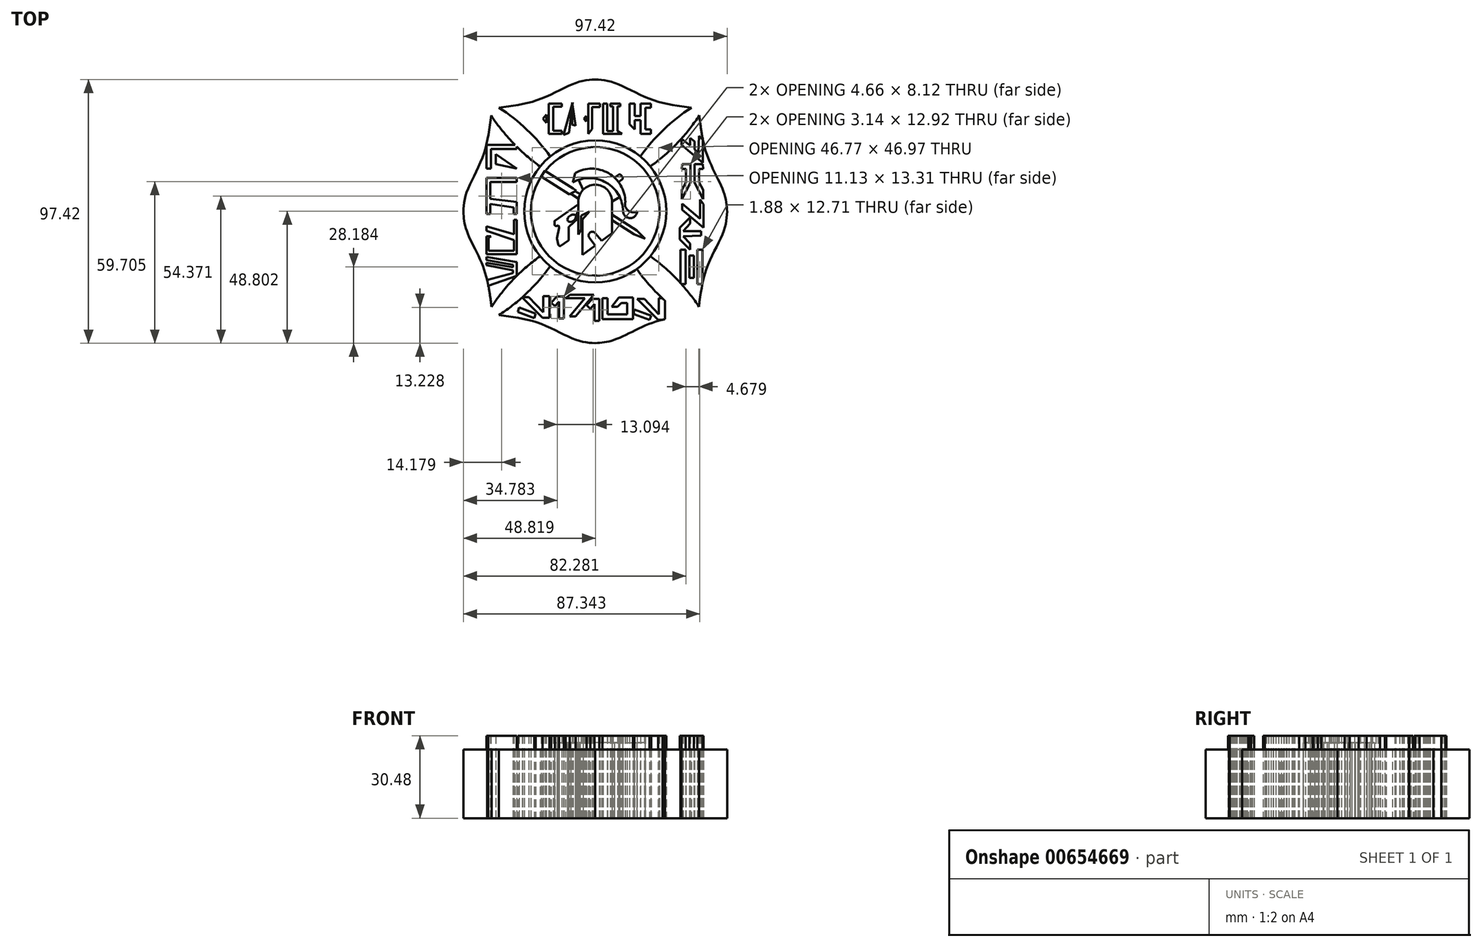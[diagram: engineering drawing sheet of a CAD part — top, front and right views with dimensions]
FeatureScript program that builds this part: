
annotation { "Feature Type Name" : "Feature", "Feature Type Description" : "" }
export const myFeature = defineFeature(function(context is Context, id is Id, definition is map)
    precondition{}
    {
        {
            var Q0;
            Q0=qCreatedBy(makeId("Top.planeOp"),FACE);
            var sketch = newSketch(context, id + "F0", { "sketchPlane" : qUnion([Q0])});
            skCircle(sketch, "E0", {"center": v(0, 0) * mm, "radius": 26.23 * mm});
            skCircle(sketch, "E1", {"center": v(0, 0) * mm, "radius": 23.74 * mm});
            skArc(sketch, "E2", {"start": v(35.51, 38.32) * mm, "mid": v(25.23, 30.18) * mm, "end": v(16.63, 20.3) * mm});
            skArc(sketch, "E3.MirrorCS", {"start": v(38.41, 35.41) * mm, "mid": v(30.25, 25.15) * mm, "end": v(20.34, 16.57) * mm});
            skArc(sketch, "E4.MirrorCS", {"start": v(-35.51, 38.32) * mm, "mid": v(-25.23, 30.18) * mm, "end": v(-16.63, 20.3) * mm});
            skArc(sketch, "E5.MirrorCS", {"start": v(-38.41, 35.41) * mm, "mid": v(-30.25, 25.15) * mm, "end": v(-20.34, 16.57) * mm});
            skArc(sketch, "E6.MirrorCS", {"start": v(-35.51, -38.32) * mm, "mid": v(-25.23, -30.18) * mm, "end": v(-16.63, -20.3) * mm});
            skArc(sketch, "E7.MirrorCS", {"start": v(-38.41, -35.41) * mm, "mid": v(-30.25, -25.15) * mm, "end": v(-20.34, -16.57) * mm});
            skArc(sketch, "E8.MirrorCS", {"start": v(38.41, -35.41) * mm, "mid": v(30.25, -25.15) * mm, "end": v(20.34, -16.57) * mm});
            skFitSpline(sketch, "E9", {"points": [v(-35.51, 38.32) * mm, v(-20.45, 41.42) * mm, v(-6.98, 47.51) * mm, v(0, 48.72) * mm], "startDerivative": vector(40.3, 5.04) * mm, "endDerivative": vector(25.56, 1.65) * mm});
            skFitSpline(sketch, "E10.MirrorCS", {"points": [v(35.51, 38.32) * mm, v(20.45, 41.42) * mm, v(6.98, 47.51) * mm, v(0, 48.72) * mm], "startDerivative": vector(-40.3, 5.04) * mm, "endDerivative": vector(-25.56, 1.65) * mm});
            skFitSpline(sketch, "E11.MirrorCS", {"points": [v(38.41, 35.41) * mm, v(41.47, 20.34) * mm, v(47.53, 6.86) * mm, v(48.72, -0.14) * mm], "startDerivative": vector(4.94, -40.31) * mm, "endDerivative": vector(1.58, -25.56) * mm});
            skFitSpline(sketch, "E12.MirrorCS", {"points": [v(38.23, -35.61) * mm, v(41.37, -20.55) * mm, v(47.5, -7.1) * mm, v(48.72, -0.12) * mm], "startDerivative": vector(5.15, 40.29) * mm, "endDerivative": vector(1.72, 25.55) * mm});
            skArc(sketch, "E13.MirrorCS", {"start": v(34.27, -39.56) * mm, "mid": v(24, -31.4) * mm, "end": v(15.43, -21.48) * mm});
            skFitSpline(sketch, "E14.MirrorCS", {"points": [v(35.51, -38.32) * mm, v(20.45, -41.42) * mm, v(6.98, -47.51) * mm, v(0, -48.72) * mm], "startDerivative": vector(-40.3, -5.04) * mm, "endDerivative": vector(-25.56, -1.65) * mm});
            skFitSpline(sketch, "E15.MirrorCS", {"points": [v(-35.51, -38.32) * mm, v(-20.45, -41.42) * mm, v(-6.98, -47.51) * mm, v(0, -48.72) * mm], "startDerivative": vector(40.3, -5.04) * mm, "endDerivative": vector(25.56, -1.65) * mm});
            skFitSpline(sketch, "E16.MirrorCS", {"points": [v(-38.23, -35.61) * mm, v(-41.37, -20.55) * mm, v(-47.5, -7.1) * mm, v(-48.72, -0.12) * mm], "startDerivative": vector(-5.15, 40.29) * mm, "endDerivative": vector(-1.72, 25.55) * mm});
            skFitSpline(sketch, "E17.MirrorCS", {"points": [v(-38.41, 35.41) * mm, v(-41.47, 20.34) * mm, v(-47.53, 6.86) * mm, v(-48.72, -0.14) * mm], "startDerivative": vector(-4.94, -40.31) * mm, "endDerivative": vector(-1.58, -25.56) * mm});
            skLineSegment(sketch, "E18.left", {"start": v(-6.25, 3.57) * mm, "end": v(-6.25, -8.57) * mm});
            skLineSegment(sketch, "E18.right", {"start": v(6.25, 3.57) * mm, "end": v(6.25, -8.06) * mm});
            skPoint(sketch, "E18.middle", {"position": v(0, -8.06) * mm});
            skArc(sketch, "E19", {"start": v(6.25, 3.57) * mm, "mid": v(0, 9.82) * mm, "end": v(-6.25, 3.57) * mm});
            skLineSegment(sketch, "E20", {"start": v(-4.67, -16.13) * mm, "end": v(0, -12.68) * mm});
            skLineSegment(sketch, "E21", {"start": v(2.37, -10.93) * mm, "end": v(0, -8.06) * mm});
            skLineSegment(sketch, "E22", {"start": v(0, -12.68) * mm, "end": v(-2.14, -9.78) * mm});
            skArc(sketch, "E23", {"start": v(0, -8.06) * mm, "mid": v(-1.93, -7.85) * mm, "end": v(-2.14, -9.78) * mm});
            skPoint(sketch, "E23.third.point", {"position": v(0, -9.78) * mm});
            skLineSegment(sketch, "E24.trimOffspring", {"start": v(2.37, -10.93) * mm, "end": v(6.25, -8.06) * mm});
            skPoint(sketch, "E18.top.end.orphan", {"position": v(6.25, -19.7) * mm});
            skPoint(sketch, "E25.orphan", {"position": v(-6.25, -19.7) * mm});
            skArc(sketch, "E26", {"start": v(11.12, 3.49) * mm, "mid": v(4.91, 14.1) * mm, "end": v(-7.38, 14.17) * mm});
            skArc(sketch, "E27", {"start": v(10.28, 0.03) * mm, "mid": v(4.07, 10.64) * mm, "end": v(-8.22, 10.7) * mm});
            skLineSegment(sketch, "E28", {"start": v(-8.22, 10.7) * mm, "end": v(-7.38, 14.17) * mm});
            skArc(sketch, "E29", {"start": v(11.12, 3.49) * mm, "mid": v(12.15, 0.3) * mm, "end": v(15.48, 0.03) * mm});
            skArc(sketch, "E30", {"start": v(10.28, 0.03) * mm, "mid": v(12.88, -2.5) * mm, "end": v(15.48, 0.03) * mm});
            skLineSegment(sketch, "E31", {"start": v(15.43, -21.48) * mm, "end": v(15.3, -21.3) * mm});
            skLineSegment(sketch, "E32", {"start": v(-4.67, -16.13) * mm, "end": v(-4.67, -2.97) * mm});
            skLineSegment(sketch, "E33", {"start": v(-4.67, -2.97) * mm, "end": v(-2.14, -0.12) * mm});
            skLineSegment(sketch, "E34", {"start": v(-2.14, -0.12) * mm, "end": v(-5.26, -1.55) * mm});
            skPoint(sketch, "E34.endSnap0", {"position": v(-3.4, -1.55) * mm});
            skLineSegment(sketch, "E35", {"start": v(-5.26, -1.55) * mm, "end": v(-5.26, -6.86) * mm});
            skPoint(sketch, "E35.endSnap0", {"position": v(-6.25, -6.86) * mm});
            skLineSegment(sketch, "E36", {"start": v(-5.26, -6.86) * mm, "end": v(-6.25, -8.57) * mm});
            skPoint(sketch, "E37.orphan", {"position": v(-6.25, -17.3) * mm});
            skLineSegment(sketch, "E38", {"start": v(-4.46, 7.95) * mm, "end": v(-6.14, 11.64) * mm});
            skLineSegment(sketch, "E39", {"start": v(6.25, 3.57) * mm, "end": v(9.04, 5.3) * mm});
            skLineSegment(sketch, "E40.bottom", {"start": v(-12.4, 39.78) * mm, "end": v(-17.13, 39.78) * mm});
            skLineSegment(sketch, "E40.top", {"start": v(-12.4, 38.6) * mm, "end": v(-15.49, 38.6) * mm});
            skLineSegment(sketch, "E40.left", {"start": v(-12.4, 39.78) * mm, "end": v(-12.4, 38.6) * mm});
            skLineSegment(sketch, "E40.right", {"start": v(-17.13, 39.78) * mm, "end": v(-17.13, 38.6) * mm});
            skLineSegment(sketch, "E41.bottom", {"start": v(-17.13, 39.78) * mm, "end": v(-15.49, 39.78) * mm});
            skLineSegment(sketch, "E41.left", {"start": v(-17.13, 39.78) * mm, "end": v(-17.13, 34.21) * mm});
            skLineSegment(sketch, "E41.right", {"start": v(-15.49, 38.6) * mm, "end": v(-15.49, 34.21) * mm});
            skLineSegment(sketch, "E42.bottom", {"start": v(-2.52, 39.78) * mm, "end": v(-1.13, 39.78) * mm});
            skLineSegment(sketch, "E42.left", {"start": v(-2.52, 39.78) * mm, "end": v(-2.52, 34.21) * mm});
            skLineSegment(sketch, "E42.right", {"start": v(-1.13, 38.54) * mm, "end": v(-1.13, 34.21) * mm});
            skLineSegment(sketch, "E43.bottom", {"start": v(-2.52, 39.78) * mm, "end": v(1.82, 39.78) * mm});
            skLineSegment(sketch, "E43.top", {"start": v(-1.13, 38.54) * mm, "end": v(1.82, 38.54) * mm});
            skLineSegment(sketch, "E43.left", {"start": v(-2.52, 39.78) * mm, "end": v(-2.52, 38.54) * mm});
            skLineSegment(sketch, "E43.right", {"start": v(1.82, 39.78) * mm, "end": v(1.82, 38.54) * mm});
            skLineSegment(sketch, "E44", {"start": v(-8.28, 40.2) * mm, "end": v(-8.4, 39.75) * mm});
            skLineSegment(sketch, "E45", {"start": v(-11.7, 28.2) * mm, "end": v(-9.65, 28.98) * mm});
            skLineSegment(sketch, "E46", {"start": v(-9.65, 28.98) * mm, "end": v(-8.48, 38.58) * mm});
            skLineSegment(sketch, "E47", {"start": v(-8.48, 40.2) * mm, "end": v(-8.48, 39.51) * mm});
            skLineSegment(sketch, "E48", {"start": v(-8.48, 32.05) * mm, "end": v(-7.25, 31.7) * mm});
            skLineSegment(sketch, "E49", {"start": v(-7.25, 31.7) * mm, "end": v(-8.37, 39.46) * mm});
            skLineSegment(sketch, "E50.MirrorCS", {"start": v(-12.4, 28.65) * mm, "end": v(-17.13, 28.65) * mm});
            skLineSegment(sketch, "E51.MirrorCS", {"start": v(-12.4, 29.82) * mm, "end": v(-15.49, 29.82) * mm});
            skLineSegment(sketch, "E52.MirrorCS", {"start": v(-12.4, 28.65) * mm, "end": v(-12.4, 29.82) * mm});
            skLineSegment(sketch, "E53.MirrorCS", {"start": v(-17.13, 28.65) * mm, "end": v(-17.13, 34.21) * mm});
            skLineSegment(sketch, "E54.MirrorCS", {"start": v(-15.49, 29.82) * mm, "end": v(-15.49, 34.21) * mm});
            skLineSegment(sketch, "E55.MirrorCS", {"start": v(-2.52, 28.65) * mm, "end": v(-2.52, 34.21) * mm});
            skLineSegment(sketch, "E56.MirrorCS", {"start": v(-1.13, 30.44) * mm, "end": v(-1.13, 34.21) * mm});
            skLineSegment(sketch, "E57", {"start": v(-2.52, 28.65) * mm, "end": v(-1.13, 30.44) * mm});
            skPoint(sketch, "E58.orphan", {"position": v(-1.13, 28.65) * mm});
            skPoint(sketch, "E59.orphan", {"position": v(10.7, 28.65) * mm});
            skPoint(sketch, "E60.orphan", {"position": v(10.28, 29.44) * mm});
            skLineSegment(sketch, "E61", {"start": v(-3.29, 35.2) * mm, "end": v(-3.29, 34.21) * mm});
            skPoint(sketch, "E61.endSnap0", {"position": v(-18.03, 34.21) * mm});
            skLineSegment(sketch, "E62", {"start": v(-4.27, 34.21) * mm, "end": v(-3.29, 35.2) * mm});
            skLineSegment(sketch, "E63.MirrorCS", {"start": v(-3.29, 33.23) * mm, "end": v(-3.29, 34.21) * mm});
            skLineSegment(sketch, "E64.MirrorCS", {"start": v(-4.27, 34.21) * mm, "end": v(-3.29, 33.23) * mm});
            skLineSegment(sketch, "E65", {"start": v(-18.03, 35.71) * mm, "end": v(-19.33, 34.21) * mm});
            skLineSegment(sketch, "E66", {"start": v(-18.03, 34.21) * mm, "end": v(-18.03, 35.71) * mm});
            skLineSegment(sketch, "E67", {"start": v(-18.03, 34.21) * mm, "end": v(-18.03, 32.71) * mm});
            skLineSegment(sketch, "E68", {"start": v(-18.03, 32.71) * mm, "end": v(-19.33, 34.21) * mm});
            skLineSegment(sketch, "E69.bottom", {"start": v(2.96, 39.78) * mm, "end": v(4.44, 39.78) * mm});
            skLineSegment(sketch, "E69.top", {"start": v(2.96, 28.65) * mm, "end": v(4.44, 28.65) * mm});
            skLineSegment(sketch, "E69.left", {"start": v(2.96, 39.78) * mm, "end": v(2.96, 28.65) * mm});
            skLineSegment(sketch, "E69.right", {"start": v(4.44, 39.78) * mm, "end": v(4.44, 29.7) * mm});
            skLineSegment(sketch, "E70.bottom", {"start": v(2.96, 28.65) * mm, "end": v(8.18, 28.65) * mm});
            skLineSegment(sketch, "E70.top", {"start": v(4.44, 29.7) * mm, "end": v(6.61, 29.7) * mm});
            skLineSegment(sketch, "E70.left", {"start": v(2.96, 28.65) * mm, "end": v(2.96, 29.7) * mm});
            skLineSegment(sketch, "E71.bottom", {"start": v(8.18, 28.65) * mm, "end": v(6.61, 28.65) * mm});
            skLineSegment(sketch, "E71.top", {"start": v(8.18, 39.78) * mm, "end": v(6.61, 39.78) * mm});
            skLineSegment(sketch, "E71.left", {"start": v(8.18, 29.7) * mm, "end": v(8.18, 38.83) * mm});
            skLineSegment(sketch, "E71.right", {"start": v(6.61, 29.7) * mm, "end": v(6.61, 38.83) * mm});
            skLineSegment(sketch, "E72.bottom", {"start": v(5.53, 39.78) * mm, "end": v(9.3, 39.78) * mm});
            skLineSegment(sketch, "E72.top", {"start": v(5.53, 38.83) * mm, "end": v(6.61, 38.83) * mm});
            skLineSegment(sketch, "E72.left", {"start": v(5.53, 39.78) * mm, "end": v(5.53, 38.83) * mm});
            skLineSegment(sketch, "E72.right", {"start": v(9.3, 39.78) * mm, "end": v(9.3, 38.83) * mm});
            skLineSegment(sketch, "E73", {"start": v(8.18, 29.7) * mm, "end": v(9.87, 28.65) * mm});
            skLineSegment(sketch, "E74", {"start": v(9.87, 28.65) * mm, "end": v(8.18, 28.65) * mm});
            skLineSegment(sketch, "E75.trimOffspring", {"start": v(8.18, 38.83) * mm, "end": v(9.3, 38.83) * mm});
            skLineSegment(sketch, "E76", {"start": v(12.66, 39.78) * mm, "end": v(14.62, 39.78) * mm});
            skLineSegment(sketch, "E77.left", {"start": v(12.66, 39.78) * mm, "end": v(12.66, 32.13) * mm});
            skLineSegment(sketch, "E77.right", {"start": v(14.62, 39.78) * mm, "end": v(14.62, 35.22) * mm});
            skLineSegment(sketch, "E78.bottom", {"start": v(14.62, 35.22) * mm, "end": v(16.76, 35.22) * mm});
            skLineSegment(sketch, "E78.top", {"start": v(14.62, 33.67) * mm, "end": v(16.76, 33.67) * mm});
            skLineSegment(sketch, "E78.left", {"start": v(12.66, 35.22) * mm, "end": v(12.66, 33.67) * mm});
            skLineSegment(sketch, "E79.bottom", {"start": v(16.76, 39.78) * mm, "end": v(18.48, 39.78) * mm});
            skLineSegment(sketch, "E79.top", {"start": v(16.76, 28.65) * mm, "end": v(18.48, 28.65) * mm});
            skLineSegment(sketch, "E79.left", {"start": v(16.76, 39.78) * mm, "end": v(16.76, 35.22) * mm});
            skLineSegment(sketch, "E79.right", {"start": v(18.48, 38.24) * mm, "end": v(18.48, 30.3) * mm});
            skLineSegment(sketch, "E80.bottom", {"start": v(16.76, 39.78) * mm, "end": v(20.61, 39.78) * mm});
            skLineSegment(sketch, "E80.top", {"start": v(18.48, 38.24) * mm, "end": v(20.61, 38.24) * mm});
            skLineSegment(sketch, "E80.left", {"start": v(16.76, 39.78) * mm, "end": v(16.76, 38.24) * mm});
            skLineSegment(sketch, "E80.right", {"start": v(20.61, 39.78) * mm, "end": v(20.61, 38.24) * mm});
            skLineSegment(sketch, "E81.bottom", {"start": v(16.76, 28.65) * mm, "end": v(20.61, 28.65) * mm});
            skLineSegment(sketch, "E81.top", {"start": v(18.48, 30.3) * mm, "end": v(20.61, 30.3) * mm});
            skLineSegment(sketch, "E81.left", {"start": v(16.76, 28.65) * mm, "end": v(16.76, 30.3) * mm});
            skLineSegment(sketch, "E81.right", {"start": v(20.61, 28.65) * mm, "end": v(20.61, 30.3) * mm});
            skLineSegment(sketch, "E82.trimOffspring", {"start": v(18.48, 28.65) * mm, "end": v(20.61, 28.65) * mm});
            skLineSegment(sketch, "E83", {"start": v(12.66, 32.13) * mm, "end": v(14.62, 30.23) * mm});
            skLineSegment(sketch, "E84.trimOffspring", {"start": v(16.76, 33.67) * mm, "end": v(16.76, 28.65) * mm});
            skLineSegment(sketch, "E85.trimOffspring", {"start": v(14.62, 33.67) * mm, "end": v(14.62, 30.23) * mm});
            skLineSegment(sketch, "E86.trimOffspring", {"start": v(-8.4, 39.75) * mm, "end": v(-8.48, 40.2) * mm});
            skLineSegment(sketch, "E87.trimOffspring", {"start": v(-8.48, 39.51) * mm, "end": v(-11.7, 28.2) * mm});
            skLineSegment(sketch, "E88.trimOffspring", {"start": v(-8.37, 39.46) * mm, "end": v(-8.28, 40.2) * mm});
            skLineSegment(sketch, "E89.trimOffspring", {"start": v(-8.48, 38.58) * mm, "end": v(-8.48, 32.05) * mm});
            skLineSegment(sketch, "E90", {"start": v(-28.97, -18.8) * mm, "end": v(-40.1, -16.82) * mm});
            skLineSegment(sketch, "E91", {"start": v(-40.1, -16.82) * mm, "end": v(-40.1, -18.04) * mm});
            skLineSegment(sketch, "E92", {"start": v(-40.1, -18.04) * mm, "end": v(-30.4, -19.76) * mm});
            skLineSegment(sketch, "E93", {"start": v(-30.4, -19.76) * mm, "end": v(-30.4, -20.72) * mm});
            skLineSegment(sketch, "E94", {"start": v(-30.4, -20.72) * mm, "end": v(-40.1, -19) * mm});
            skLineSegment(sketch, "E95", {"start": v(-40.1, -19) * mm, "end": v(-40.1, -19.9) * mm});
            skLineSegment(sketch, "E96", {"start": v(-40.1, -19.9) * mm, "end": v(-30.32, -21.8) * mm});
            skLineSegment(sketch, "E97", {"start": v(-30.32, -21.8) * mm, "end": v(-30.32, -22.87) * mm});
            skLineSegment(sketch, "E98", {"start": v(-30.32, -22.87) * mm, "end": v(-40.1, -25.47) * mm});
            skLineSegment(sketch, "E99", {"start": v(-40.1, -25.47) * mm, "end": v(-40.1, -27.73) * mm});
            skLineSegment(sketch, "E100", {"start": v(-40.1, -27.73) * mm, "end": v(-28.97, -23.85) * mm});
            skLineSegment(sketch, "E101", {"start": v(-28.97, -23.85) * mm, "end": v(-28.97, -18.8) * mm});
            skLineSegment(sketch, "E102.bottom", {"start": v(-40.1, -15.83) * mm, "end": v(-40.1, -14.56) * mm});
            skLineSegment(sketch, "E102.left", {"start": v(-40.1, -15.83) * mm, "end": v(-28.97, -15.83) * mm});
            skLineSegment(sketch, "E102.right", {"start": v(-39.41, -14.56) * mm, "end": v(-30.02, -14.56) * mm});
            skLineSegment(sketch, "E103.bottom", {"start": v(-28.97, -15.83) * mm, "end": v(-28.97, -3.12) * mm});
            skLineSegment(sketch, "E103.top", {"start": v(-30.02, -14.56) * mm, "end": v(-30.02, -10.64) * mm});
            skLineSegment(sketch, "E103.left", {"start": v(-28.97, -15.83) * mm, "end": v(-30.02, -15.83) * mm});
            skLineSegment(sketch, "E103.right", {"start": v(-28.97, -3.12) * mm, "end": v(-30.02, -3.12) * mm});
            skLineSegment(sketch, "E104.left", {"start": v(-38.1, -6.34) * mm, "end": v(-38.11, -6.34) * mm});
            skLineSegment(sketch, "E104.right", {"start": v(-38.1, -5.52) * mm, "end": v(-38.11, -5.52) * mm});
            skLineSegment(sketch, "E105.bottom", {"start": v(-40.1, -15.83) * mm, "end": v(-40.1, -9.27) * mm});
            skLineSegment(sketch, "E105.top", {"start": v(-39.41, -14.56) * mm, "end": v(-39.41, -9.91) * mm});
            skLineSegment(sketch, "E105.left", {"start": v(-40.1, -15.83) * mm, "end": v(-39.41, -15.83) * mm});
            skLineSegment(sketch, "E105.right", {"start": v(-40.1, -9.27) * mm, "end": v(-39.41, -9.27) * mm});
            skLineSegment(sketch, "E106", {"start": v(-40.1, -9.27) * mm, "end": v(-38.43, -9.27) * mm});
            skPoint(sketch, "E106.endSnap0", {"position": v(-39.75, -9.27) * mm});
            skLineSegment(sketch, "E107", {"start": v(-38.43, -9.27) * mm, "end": v(-39.41, -9.91) * mm});
            skLineSegment(sketch, "E108", {"start": v(-30.02, -10.64) * mm, "end": v(-40.1, -7.24) * mm});
            skLineSegment(sketch, "E109", {"start": v(-40.1, -7.24) * mm, "end": v(-40.1, -5.52) * mm});
            skLineSegment(sketch, "E110", {"start": v(-40.1, -5.52) * mm, "end": v(-30.02, -8.5) * mm});
            skLineSegment(sketch, "E111.bottom", {"start": v(-28.97, -0.92) * mm, "end": v(-28.97, 3.44) * mm});
            skLineSegment(sketch, "E111.top", {"start": v(-30.13, -0.92) * mm, "end": v(-30.13, 1.44) * mm});
            skLineSegment(sketch, "E111.left", {"start": v(-28.97, -0.92) * mm, "end": v(-30.13, -0.92) * mm});
            skLineSegment(sketch, "E111.right", {"start": v(-28.97, 3.44) * mm, "end": v(-30.13, 3.44) * mm});
            skLineSegment(sketch, "E112", {"start": v(-30.13, 1.44) * mm, "end": v(-38.78, 2.72) * mm});
            skLineSegment(sketch, "E113", {"start": v(-40.1, 2.92) * mm, "end": v(-40.1, 4.72) * mm});
            skLineSegment(sketch, "E114", {"start": v(-38.78, 4.57) * mm, "end": v(-28.97, 3.44) * mm});
            skLineSegment(sketch, "E115.bottom", {"start": v(-40.1, -1) * mm, "end": v(-40.1, 12.32) * mm});
            skLineSegment(sketch, "E115.top", {"start": v(-38.78, -1) * mm, "end": v(-38.78, 2.72) * mm});
            skLineSegment(sketch, "E115.left", {"start": v(-40.1, -1) * mm, "end": v(-38.78, -1) * mm});
            skLineSegment(sketch, "E115.right", {"start": v(-40.1, 12.32) * mm, "end": v(-38.78, 12.32) * mm});
            skLineSegment(sketch, "E116.bottom", {"start": v(-40.1, 12.32) * mm, "end": v(-40.1, 10.89) * mm});
            skLineSegment(sketch, "E116.top", {"start": v(-28.97, 12.32) * mm, "end": v(-28.97, 10.89) * mm});
            skLineSegment(sketch, "E116.left", {"start": v(-40.1, 12.32) * mm, "end": v(-28.97, 12.32) * mm});
            skLineSegment(sketch, "E116.right", {"start": v(-38.78, 10.89) * mm, "end": v(-28.97, 10.89) * mm});
            skLineSegment(sketch, "E117", {"start": v(-40.1, 15.79) * mm, "end": v(-40.1, 24.5) * mm});
            skLineSegment(sketch, "E118.top", {"start": v(-38.46, 15.79) * mm, "end": v(-38.46, 22.98) * mm});
            skLineSegment(sketch, "E118.left", {"start": v(-40.1, 15.79) * mm, "end": v(-38.46, 15.79) * mm});
            skLineSegment(sketch, "E118.right", {"start": v(-40.1, 24.5) * mm, "end": v(-38.46, 24.5) * mm});
            skLineSegment(sketch, "E119.bottom", {"start": v(-40.1, 24.5) * mm, "end": v(-40.1, 22.98) * mm});
            skLineSegment(sketch, "E119.top", {"start": v(-29, 24.5) * mm, "end": v(-29, 22.98) * mm});
            skLineSegment(sketch, "E119.left", {"start": v(-40.1, 24.5) * mm, "end": v(-29, 24.5) * mm});
            skLineSegment(sketch, "E119.right", {"start": v(-38.46, 22.98) * mm, "end": v(-29, 22.98) * mm});
            skLineSegment(sketch, "E120", {"start": v(-28.97, 15.79) * mm, "end": v(-36.7, 17.48) * mm});
            skLineSegment(sketch, "E121", {"start": v(-36.7, 17.48) * mm, "end": v(-36.7, 21.15) * mm});
            skLineSegment(sketch, "E122", {"start": v(-36.7, 21.15) * mm, "end": v(-28.97, 15.79) * mm});
            skLineSegment(sketch, "E123.trimOffspring", {"start": v(-38.78, 4.57) * mm, "end": v(-38.78, 10.89) * mm});
            skLineSegment(sketch, "E124.trimOffspring", {"start": v(-30.02, -8.5) * mm, "end": v(-30.02, -3.12) * mm});
            skPoint(sketch, "E125.orphan", {"position": v(-40.1, -23.85) * mm});
            skPoint(sketch, "E126.orphan", {"position": v(-28.97, 1.26) * mm});
            skLineSegment(sketch, "E127.bottom", {"start": v(-19.94, 12.89) * mm, "end": v(-9.54, 6.25) * mm});
            skLineSegment(sketch, "E127.top", {"start": v(-18.56, 15.04) * mm, "end": v(-8.17, 8.4) * mm});
            skLineSegment(sketch, "E127.left", {"start": v(-19.94, 12.89) * mm, "end": v(-18.56, 15.04) * mm});
            skLineSegment(sketch, "E127.right", {"start": v(-9.54, 6.25) * mm, "end": v(-8.17, 8.4) * mm});
            skLineSegment(sketch, "E128", {"start": v(-5.9, 6.52) * mm, "end": v(-5.6, 6.34) * mm});
            skLineSegment(sketch, "E129", {"start": v(-7.93, 5.76) * mm, "end": v(-6.16, 4.63) * mm});
            skLineSegment(sketch, "E130", {"start": v(14.39, -8.5) * mm, "end": v(18.41, -10.1) * mm});
            skPoint(sketch, "E130.endSnap0", {"position": v(-81.83, -16.44) * mm});
            skLineSegment(sketch, "E131", {"start": v(18.41, -10.1) * mm, "end": v(15.32, -7.03) * mm});
            skLineSegment(sketch, "E132.0", {"start": v(14.39, -8.5) * mm, "end": v(15.32, -7.03) * mm, "construction": true});
            skLineSegment(sketch, "E133.trimOffspring", {"start": v(6.25, -1.24) * mm, "end": v(15.32, -7.03) * mm});
            skLineSegment(sketch, "E134.trimOffspring", {"start": v(6.25, -3.3) * mm, "end": v(14.39, -8.5) * mm});
            skLineSegment(sketch, "E135", {"start": v(-9.54, 6.25) * mm, "end": v(-7.04, 7.6) * mm});
            skPoint(sketch, "E135.endSnap0", {"position": v(-7.04, 5.2) * mm});
            skLineSegment(sketch, "E136", {"start": v(-7.04, 7.6) * mm, "end": v(-8.17, 8.4) * mm});
            skLineSegment(sketch, "E137", {"start": v(-5.9, 6.52) * mm, "end": v(-7.34, 7.44) * mm});
            skLineSegment(sketch, "E138", {"start": v(-7.93, 5.76) * mm, "end": v(-9.08, 6.5) * mm});
            skLineSegment(sketch, "E139", {"start": v(-9.76, -10.38) * mm, "end": v(-9.76, -5.95) * mm});
            skLineSegment(sketch, "E140", {"start": v(-9.56, -5.5) * mm, "end": v(-6.53, -2.75) * mm});
            skLineSegment(sketch, "E141", {"start": v(-6.35, -2.14) * mm, "end": v(-6.69, -0.96) * mm});
            skLineSegment(sketch, "E142", {"start": v(-6.46, -0.3) * mm, "end": v(-6.25, -0.16) * mm});
            skLineSegment(sketch, "E143", {"start": v(-10.01, -10.87) * mm, "end": v(-12.63, -12.7) * mm});
            skLineSegment(sketch, "E144", {"start": v(-13.55, -12.37) * mm, "end": v(-14.15, -10.12) * mm});
            skLineSegment(sketch, "E145", {"start": v(-14.15, -9.83) * mm, "end": v(-13.33, -6.24) * mm});
            skLineSegment(sketch, "E146", {"start": v(-13.33, -5.94) * mm, "end": v(-13.56, -5.15) * mm});
            skLineSegment(sketch, "E147", {"start": v(-13.56, -5.15) * mm, "end": v(-14.29, -5.36) * mm});
            skLineSegment(sketch, "E148", {"start": v(-15.05, -4.78) * mm, "end": v(-15.05, -3.9) * mm});
            skLineSegment(sketch, "E149", {"start": v(-14.8, -3.4) * mm, "end": v(-6.25, 2.58) * mm});
            skLineSegment(sketch, "E150", {"start": v(8.64, 10.79) * mm, "end": v(9.96, 11.84) * mm});
            skLineSegment(sketch, "E151", {"start": v(10.06, 12.68) * mm, "end": v(9.46, 13.43) * mm});
            skLineSegment(sketch, "E152", {"start": v(8.65, 13.55) * mm, "end": v(7.08, 12.46) * mm});
            skEllipse(sketch, "E153", {"center": v(-8.66, -2.52) * mm, "majorRadius": 1.77 * mm, "minorRadius": 1.1 * mm, "majorAxis": v(0.82, 0.57)});
            skPoint(sketch, "E154.visualSharp", {"position": v(-13.33, -13.2) * mm});
            skArc(sketch, "E154.filletArc", {"start": v(-13.55, -12.37) * mm, "mid": v(-13.18, -12.78) * mm, "end": v(-12.63, -12.7) * mm});
            skPoint(sketch, "E155.visualSharp", {"position": v(-9.76, -10.7) * mm});
            skArc(sketch, "E155.filletArc", {"start": v(-10.01, -10.87) * mm, "mid": v(-9.83, -10.66) * mm, "end": v(-9.76, -10.38) * mm});
            skPoint(sketch, "E156.visualSharp", {"position": v(-9.76, -5.69) * mm});
            skArc(sketch, "E156.filletArc", {"start": v(-9.56, -5.5) * mm, "mid": v(-9.7, -5.7) * mm, "end": v(-9.76, -5.95) * mm});
            skPoint(sketch, "E157.visualSharp", {"position": v(-6.25, -2.5) * mm});
            skArc(sketch, "E157.filletArc", {"start": v(-6.53, -2.75) * mm, "mid": v(-6.35, -2.47) * mm, "end": v(-6.35, -2.14) * mm});
            skPoint(sketch, "E158.visualSharp", {"position": v(-6.8, -0.54) * mm});
            skArc(sketch, "E158.filletArc", {"start": v(-6.46, -0.3) * mm, "mid": v(-6.68, -0.6) * mm, "end": v(-6.69, -0.96) * mm});
            skPoint(sketch, "E159.visualSharp", {"position": v(-14.18, -9.98) * mm});
            skArc(sketch, "E159.filletArc", {"start": v(-14.15, -9.83) * mm, "mid": v(-14.17, -9.98) * mm, "end": v(-14.15, -10.12) * mm});
            skPoint(sketch, "E160.visualSharp", {"position": v(-13.3, -6.09) * mm});
            skArc(sketch, "E160.filletArc", {"start": v(-13.33, -6.24) * mm, "mid": v(-13.31, -6.09) * mm, "end": v(-13.33, -5.94) * mm});
            skPoint(sketch, "E161.visualSharp", {"position": v(-15.05, -5.58) * mm});
            skArc(sketch, "E161.filletArc", {"start": v(-15.05, -4.78) * mm, "mid": v(-14.81, -5.26) * mm, "end": v(-14.29, -5.36) * mm});
            skPoint(sketch, "E162.visualSharp", {"position": v(-15.05, -3.59) * mm});
            skArc(sketch, "E162.filletArc", {"start": v(-14.8, -3.4) * mm, "mid": v(-14.98, -3.62) * mm, "end": v(-15.05, -3.9) * mm});
            skPoint(sketch, "E163.visualSharp", {"position": v(10.43, 12.21) * mm});
            skArc(sketch, "E163.filletArc", {"start": v(9.96, 11.84) * mm, "mid": v(10.19, 12.24) * mm, "end": v(10.06, 12.68) * mm});
            skPoint(sketch, "E164.visualSharp", {"position": v(9.11, 13.88) * mm});
            skArc(sketch, "E164.filletArc", {"start": v(9.46, 13.43) * mm, "mid": v(9.08, 13.65) * mm, "end": v(8.65, 13.55) * mm});
            skLineSegment(sketch, "E165", {"start": v(38.28, 27.89) * mm, "end": v(39.78, 26.46) * mm});
            skLineSegment(sketch, "E166", {"start": v(39.78, 26.46) * mm, "end": v(39.78, 17.96) * mm});
            skLineSegment(sketch, "E167", {"start": v(39.78, 17.96) * mm, "end": v(31.81, 24.58) * mm});
            skLineSegment(sketch, "E168", {"start": v(31.81, 24.58) * mm, "end": v(31.81, 26.84) * mm});
            skLineSegment(sketch, "E169", {"start": v(31.81, 26.84) * mm, "end": v(35.04, 24.28) * mm});
            skLineSegment(sketch, "E170", {"start": v(35.04, 24.28) * mm, "end": v(35.04, 27.06) * mm});
            skLineSegment(sketch, "E171", {"start": v(35.04, 27.06) * mm, "end": v(36.62, 25.86) * mm});
            skLineSegment(sketch, "E172", {"start": v(36.62, 25.86) * mm, "end": v(36.62, 22.93) * mm});
            skLineSegment(sketch, "E173", {"start": v(36.62, 22.93) * mm, "end": v(38.05, 21.57) * mm});
            skLineSegment(sketch, "E174", {"start": v(38.05, 21.57) * mm, "end": v(38.28, 27.89) * mm});
            skLineSegment(sketch, "E175", {"start": v(39.77, 17.46) * mm, "end": v(36.68, 17.46) * mm});
            skLineSegment(sketch, "E176", {"start": v(36.68, 17.46) * mm, "end": v(36.68, 10.57) * mm});
            skLineSegment(sketch, "E177", {"start": v(36.68, 10.57) * mm, "end": v(39.82, 4.53) * mm});
            skLineSegment(sketch, "E178", {"start": v(39.82, 4.53) * mm, "end": v(39.82, 7.86) * mm});
            skLineSegment(sketch, "E179", {"start": v(39.82, 7.86) * mm, "end": v(38.34, 10.7) * mm});
            skLineSegment(sketch, "E180", {"start": v(38.34, 10.7) * mm, "end": v(38.34, 15.65) * mm});
            skLineSegment(sketch, "E181", {"start": v(38.34, 15.65) * mm, "end": v(39.82, 15.65) * mm});
            skLineSegment(sketch, "E182", {"start": v(39.82, 15.65) * mm, "end": v(39.77, 17.46) * mm});
            skLineSegment(sketch, "E183.MirrorCS", {"start": v(32.06, 17.46) * mm, "end": v(35.14, 17.46) * mm});
            skLineSegment(sketch, "E184.MirrorCS", {"start": v(32, 15.65) * mm, "end": v(32.06, 17.46) * mm});
            skLineSegment(sketch, "E185.MirrorCS", {"start": v(33.48, 15.65) * mm, "end": v(32, 15.65) * mm});
            skLineSegment(sketch, "E186.MirrorCS", {"start": v(35.14, 17.46) * mm, "end": v(35.14, 10.57) * mm});
            skLineSegment(sketch, "E187.MirrorCS", {"start": v(33.48, 10.7) * mm, "end": v(33.48, 15.65) * mm});
            skLineSegment(sketch, "E188.MirrorCS", {"start": v(32, 7.86) * mm, "end": v(33.48, 10.7) * mm});
            skLineSegment(sketch, "E189.MirrorCS", {"start": v(35.14, 10.57) * mm, "end": v(32, 4.53) * mm});
            skLineSegment(sketch, "E190.MirrorCS", {"start": v(32, 4.53) * mm, "end": v(32, 7.86) * mm});
            skLineSegment(sketch, "E191", {"start": v(32.06, 2.86) * mm, "end": v(32.06, 0.6) * mm});
            skLineSegment(sketch, "E192", {"start": v(32.06, 0.6) * mm, "end": v(40.03, -6.01) * mm});
            skLineSegment(sketch, "E193", {"start": v(40.03, -6.01) * mm, "end": v(40.03, 2.63) * mm});
            skLineSegment(sketch, "E194", {"start": v(40.03, 2.63) * mm, "end": v(38.7, 4.4) * mm});
            skLineSegment(sketch, "E195", {"start": v(38.7, 4.4) * mm, "end": v(38.7, -2.78) * mm});
            skLineSegment(sketch, "E196", {"start": v(38.7, -2.78) * mm, "end": v(32.06, 2.86) * mm});
            skLineSegment(sketch, "E197", {"start": v(31.2, -10.41) * mm, "end": v(31.2, -6.01) * mm});
            skLineSegment(sketch, "E198", {"start": v(31.2, -6.01) * mm, "end": v(35.04, -2.25) * mm});
            skLineSegment(sketch, "E199", {"start": v(35.04, -2.25) * mm, "end": v(35.04, -4.58) * mm});
            skLineSegment(sketch, "E200", {"start": v(35.04, -4.58) * mm, "end": v(32.48, -7.33) * mm});
            skLineSegment(sketch, "E201", {"start": v(32.48, -7.33) * mm, "end": v(39.06, -7.33) * mm});
            skLineSegment(sketch, "E202", {"start": v(39.06, -7.33) * mm, "end": v(39.06, -9.02) * mm});
            skLineSegment(sketch, "E203", {"start": v(39.06, -9.02) * mm, "end": v(32.44, -9.17) * mm});
            skLineSegment(sketch, "E204", {"start": v(32.44, -9.17) * mm, "end": v(35.04, -11.84) * mm});
            skLineSegment(sketch, "E205", {"start": v(35.04, -11.84) * mm, "end": v(35.04, -14.17) * mm});
            skLineSegment(sketch, "E206", {"start": v(35.04, -14.17) * mm, "end": v(31.2, -10.41) * mm});
            skLineSegment(sketch, "E207.bottom", {"start": v(39.57, -14.17) * mm, "end": v(39.57, -26.88) * mm});
            skLineSegment(sketch, "E207.top", {"start": v(37.7, -14.17) * mm, "end": v(37.7, -26.88) * mm});
            skLineSegment(sketch, "E207.left", {"start": v(39.57, -14.17) * mm, "end": v(37.7, -14.17) * mm});
            skLineSegment(sketch, "E207.right", {"start": v(39.57, -26.88) * mm, "end": v(37.7, -26.88) * mm});
            skLineSegment(sketch, "E208.bottom", {"start": v(36.5, -16.28) * mm, "end": v(36.5, -24.62) * mm});
            skLineSegment(sketch, "E208.top", {"start": v(34.76, -16.28) * mm, "end": v(34.76, -24.62) * mm});
            skLineSegment(sketch, "E208.left", {"start": v(36.5, -16.28) * mm, "end": v(34.76, -16.28) * mm});
            skLineSegment(sketch, "E208.right", {"start": v(36.5, -24.62) * mm, "end": v(34.76, -24.62) * mm});
            skLineSegment(sketch, "E209.bottom", {"start": v(33.33, -14.17) * mm, "end": v(33.33, -26.88) * mm});
            skLineSegment(sketch, "E209.top", {"start": v(31.45, -14.17) * mm, "end": v(31.45, -26.88) * mm});
            skLineSegment(sketch, "E209.left", {"start": v(33.33, -14.17) * mm, "end": v(31.45, -14.17) * mm});
            skLineSegment(sketch, "E209.right", {"start": v(33.33, -26.88) * mm, "end": v(31.45, -26.88) * mm});
            skLineSegment(sketch, "E210", {"start": v(-27, -31.8) * mm, "end": v(-19.4, -39.36) * mm});
            skLineSegment(sketch, "E211", {"start": v(-19.4, -39.36) * mm, "end": v(-16.9, -39.36) * mm});
            skLineSegment(sketch, "E212", {"start": v(-16.9, -39.36) * mm, "end": v(-16.9, -31.38) * mm});
            skLineSegment(sketch, "E213", {"start": v(-16.9, -31.38) * mm, "end": v(-19.18, -31.38) * mm});
            skLineSegment(sketch, "E214", {"start": v(-19.18, -31.38) * mm, "end": v(-19.18, -37.34) * mm});
            skLineSegment(sketch, "E215", {"start": v(-19.18, -37.34) * mm, "end": v(-24.5, -31.65) * mm});
            skLineSegment(sketch, "E216", {"start": v(-24.5, -31.65) * mm, "end": v(-26.81, -31.65) * mm});
            skLineSegment(sketch, "E217", {"start": v(-28.12, -35.53) * mm, "end": v(-21.95, -37.81) * mm});
            skLineSegment(sketch, "E218", {"start": v(-21.95, -37.81) * mm, "end": v(-22.53, -39.4) * mm});
            skLineSegment(sketch, "E219", {"start": v(-22.53, -39.4) * mm, "end": v(-28.62, -37.14) * mm});
            skLineSegment(sketch, "E220", {"start": v(-28.62, -37.14) * mm, "end": v(-28.12, -35.53) * mm});
            skLineSegment(sketch, "E221", {"start": v(-16.26, -33.68) * mm, "end": v(-14.08, -31.42) * mm});
            skLineSegment(sketch, "E222", {"start": v(-14.08, -31.42) * mm, "end": v(-11.6, -31.42) * mm});
            skLineSegment(sketch, "E223", {"start": v(-11.6, -31.42) * mm, "end": v(-11.6, -39.54) * mm});
            skLineSegment(sketch, "E224", {"start": v(-11.6, -39.54) * mm, "end": v(-13.33, -39.54) * mm});
            skLineSegment(sketch, "E225", {"start": v(-13.33, -39.54) * mm, "end": v(-13.33, -33.3) * mm});
            skLineSegment(sketch, "E226", {"start": v(-13.33, -33.3) * mm, "end": v(-14.9, -35.03) * mm});
            skLineSegment(sketch, "E227", {"start": v(-14.9, -35.03) * mm, "end": v(-16.26, -33.68) * mm});
            skLineSegment(sketch, "E228", {"start": v(-9.45, -38.79) * mm, "end": v(-7.2, -38.79) * mm});
            skLineSegment(sketch, "E229", {"start": v(-7.2, -38.79) * mm, "end": v(-0.58, -30.82) * mm});
            skLineSegment(sketch, "E230", {"start": v(-0.58, -30.82) * mm, "end": v(-9.23, -30.82) * mm});
            skLineSegment(sketch, "E231", {"start": v(-9.23, -30.82) * mm, "end": v(-10.98, -32.13) * mm});
            skLineSegment(sketch, "E232", {"start": v(-10.98, -32.13) * mm, "end": v(-3.81, -32.13) * mm});
            skLineSegment(sketch, "E233", {"start": v(-3.81, -32.13) * mm, "end": v(-9.45, -38.79) * mm});
            skLineSegment(sketch, "E234", {"start": v(-3.16, -34.63) * mm, "end": v(-0.98, -32.38) * mm});
            skLineSegment(sketch, "E235", {"start": v(-0.98, -32.38) * mm, "end": v(1.5, -32.38) * mm});
            skLineSegment(sketch, "E236", {"start": v(1.5, -32.38) * mm, "end": v(1.5, -40.5) * mm});
            skLineSegment(sketch, "E237", {"start": v(1.5, -40.5) * mm, "end": v(-0.23, -40.5) * mm});
            skLineSegment(sketch, "E238", {"start": v(-0.23, -40.5) * mm, "end": v(-0.23, -34.26) * mm});
            skLineSegment(sketch, "E239", {"start": v(-0.23, -34.26) * mm, "end": v(-1.81, -35.99) * mm});
            skLineSegment(sketch, "E240", {"start": v(-1.81, -35.99) * mm, "end": v(-3.16, -34.63) * mm});
            skLineSegment(sketch, "E241", {"start": v(2.64, -32.04) * mm, "end": v(2.64, -39.86) * mm});
            skLineSegment(sketch, "E242", {"start": v(2.64, -39.86) * mm, "end": v(14, -39.86) * mm});
            skLineSegment(sketch, "E243", {"start": v(14, -39.86) * mm, "end": v(14, -31.9) * mm});
            skLineSegment(sketch, "E244", {"start": v(14, -31.9) * mm, "end": v(8.77, -31.9) * mm});
            skLineSegment(sketch, "E245", {"start": v(8.77, -31.9) * mm, "end": v(6.14, -35.24) * mm});
            skLineSegment(sketch, "E246", {"start": v(6.14, -35.24) * mm, "end": v(8.24, -35.24) * mm});
            skLineSegment(sketch, "E247", {"start": v(8.24, -35.24) * mm, "end": v(9.58, -33.87) * mm});
            skLineSegment(sketch, "E248", {"start": v(9.58, -33.87) * mm, "end": v(11.85, -33.87) * mm});
            skLineSegment(sketch, "E249", {"start": v(11.85, -33.87) * mm, "end": v(11.85, -38.1) * mm});
            skLineSegment(sketch, "E250", {"start": v(11.85, -38.1) * mm, "end": v(4.6, -38.1) * mm});
            skLineSegment(sketch, "E251", {"start": v(4.6, -38.1) * mm, "end": v(4.6, -32.04) * mm});
            skLineSegment(sketch, "E252", {"start": v(4.6, -32.04) * mm, "end": v(2.64, -32.04) * mm});
            skLineSegment(sketch, "E253", {"start": v(15.45, -32.36) * mm, "end": v(23.22, -40.07) * mm});
            skLineSegment(sketch, "E254", {"start": v(23.22, -40.07) * mm, "end": v(25.71, -40.07) * mm});
            skLineSegment(sketch, "E255", {"start": v(25.71, -40.07) * mm, "end": v(25.71, -32.09) * mm});
            skLineSegment(sketch, "E256", {"start": v(25.71, -32.09) * mm, "end": v(23.43, -32.09) * mm});
            skLineSegment(sketch, "E257", {"start": v(23.43, -32.09) * mm, "end": v(23.43, -38.05) * mm});
            skLineSegment(sketch, "E258", {"start": v(23.43, -38.05) * mm, "end": v(18.11, -32.36) * mm});
            skLineSegment(sketch, "E259", {"start": v(18.11, -32.36) * mm, "end": v(15.45, -32.36) * mm});
            skLineSegment(sketch, "E260", {"start": v(14.5, -36.24) * mm, "end": v(20.66, -38.52) * mm});
            skLineSegment(sketch, "E261", {"start": v(20.66, -38.52) * mm, "end": v(20.08, -40.1) * mm});
            skLineSegment(sketch, "E262", {"start": v(20.08, -40.1) * mm, "end": v(14.4, -38) * mm});
            skLineSegment(sketch, "E263", {"start": v(14.16, -37.34) * mm, "end": v(14.5, -36.24) * mm});
            skPoint(sketch, "E264.orphan", {"position": v(-27.16, -31.65) * mm});
            skLineSegment(sketch, "E265", {"start": v(14.4, -38) * mm, "end": v(14.16, -37.34) * mm});
            skSolve(sketch);
        }
        {
            var Q0;
            Q0=makeQuery(id+"F0.imprint","IMPRINT",FACE,{"disambiguationData":[TD([[makeQuery(id+"F0.imprint","IMPRINT",EDGE,{"derivedFrom":sQuery(id+"F0.wireOp",EDGE,"E20")}),-1.0]])]});
            var Q1;
            {var subQ5=sQuery(id+"F0.wireOp",EDGE,"E2");Q1=makeQuery(id+"F0.imprint","IMPRINT",FACE,{"disambiguationData":[TD([[makeQuery(id+"F0.imprint","IMPRINT",EDGE,{"derivedFrom":subQ5}),-1.0]])]});}
            var Q2;
            Q2=makeQuery(id+"F0.imprint","IMPRINT",FACE,{"disambiguationData":[TD([[makeQuery(id+"F0.imprint","IMPRINT",EDGE,{"derivedFrom":sQuery(id+"F0.wireOp",EDGE,"E90")}),-1.0]])]});
            var Q3;
            {var subQ1=sQuery(id+"F0.wireOp",EDGE,"E7.MirrorCS");var subQ3=sQuery(id+"F0.wireOp",EDGE,"E16.MirrorCS");var subQ4=makeQuery(id+"F0.imprint","INTERSECT",VERTEX,{"derivedFrom":[subQ1,subQ3]});Q3=makeQuery(id+"F0.imprint","IMPRINT",FACE,{"disambiguationData":[TD([[makeQuery(id+"F0.imprint","IMPRINT",EDGE,{"disambiguationData":[TD([[subQ4,-1.0]])],"derivedFrom":subQ3}),-1.0]])]});}
            var Q4;
            {var subQ0=sQuery(id+"F0.wireOp",EDGE,"E14.MirrorCS");var subQ1=sQuery(id+"F0.wireOp",EDGE,"E13.MirrorCS");var subQ2=makeQuery(id+"F0.imprint","INTERSECT",VERTEX,{"derivedFrom":[subQ1,subQ0]});Q4=makeQuery(id+"F0.imprint","IMPRINT",FACE,{"disambiguationData":[TD([[makeQuery(id+"F0.imprint","IMPRINT",EDGE,{"disambiguationData":[TD([[subQ2,-1.0]])],"derivedFrom":subQ1}),1.0]])]});}
            var Q5;
            {var subQ6=sQuery(id+"F0.wireOp",EDGE,"E167");Q5=makeQuery(id+"F0.imprint","IMPRINT",FACE,{"disambiguationData":[TD([[makeQuery(id+"F0.imprint","IMPRINT",EDGE,{"derivedFrom":subQ6}),1.0]])]});}
            var Q6;
            {var subQ0=sQuery(id+"F0.wireOp",EDGE,"E169");Q6=makeQuery(id+"F0.imprint","IMPRINT",FACE,{"disambiguationData":[TD([[makeQuery(id+"F0.imprint","IMPRINT",EDGE,{"derivedFrom":subQ0}),1.0]])]});}
            var Q7;
            {var subQ14=sQuery(id+"F0.wireOp",EDGE,"E31");Q7=makeQuery(id+"F0.imprint","IMPRINT",FACE,{"disambiguationData":[TD([[makeQuery(id+"F0.imprint","IMPRINT",EDGE,{"derivedFrom":subQ14}),1.0]])]});}
            var Q8;
            Q8=makeQuery(id+"F0.imprint","IMPRINT",FACE,{"disambiguationData":[TD([[makeQuery(id+"F0.imprint","IMPRINT",EDGE,{"derivedFrom":sQuery(id+"F0.wireOp",EDGE,"E153")}),1.0]])]});
            extrude(context, id + "F1", {"entities" : qUnion([Q0, Q1, Q2, Q3, Q4, Q5, Q6, Q7, Q8]), "depth" : 25.4 * mm, "offsetDistance" : 25.4 * mm});
        }
        {
            var Q0;
            Q0=makeQuery(id+"F0.imprint","IMPRINT",FACE,{"disambiguationData":[TD([[makeQuery(id+"F0.imprint","IMPRINT",EDGE,{"derivedFrom":sQuery(id+"F0.wireOp",EDGE,"E139")}),1.0]])]});
            var Q1;
            {var subQ4=sQuery(id+"F0.wireOp",EDGE,"E128");Q1=makeQuery(id+"F0.imprint","IMPRINT",FACE,{"disambiguationData":[TD([[makeQuery(id+"F0.imprint","IMPRINT",EDGE,{"derivedFrom":subQ4}),-1.0]])]});}
            var Q2;
            Q2=makeQuery(id+"F0.imprint","IMPRINT",FACE,{"disambiguationData":[TD([[makeQuery(id+"F0.imprint","IMPRINT",EDGE,{"derivedFrom":sQuery(id+"F0.wireOp",EDGE,"E130")}),1.0]])]});
            var Q3;
            {var subQ2=sQuery(id+"F0.wireOp",EDGE,"E38");Q3=makeQuery(id+"F0.imprint","IMPRINT",FACE,{"disambiguationData":[TD([[makeQuery(id+"F0.imprint","IMPRINT",EDGE,{"derivedFrom":subQ2}),-1.0]])]});}
            var Q4;
            {var subQ4=sQuery(id+"F0.wireOp",EDGE,"E150");Q4=makeQuery(id+"F0.imprint","IMPRINT",FACE,{"disambiguationData":[TD([[makeQuery(id+"F0.imprint","IMPRINT",EDGE,{"derivedFrom":subQ4}),1.0]])]});}
            extrude(context, id + "F2", {"entities" : qUnion([Q0, Q1, Q2, Q3, Q4]), "depth" : 27.94 * mm, "offsetDistance" : 25.4 * mm});
        }
        {
            var Q0;
            {var subQ0=sQuery(id+"F0.wireOp",EDGE,"E127.bottom");Q0=makeQuery(id+"F0.imprint","IMPRINT",FACE,{"disambiguationData":[TD([[makeQuery(id+"F0.imprint","IMPRINT",EDGE,{"derivedFrom":subQ0}),1.0]])]});}
            var Q1;
            {var subQ4=sQuery(id+"F0.wireOp",EDGE,"E127.right");Q1=makeQuery(id+"F0.imprint","IMPRINT",FACE,{"disambiguationData":[TD([[makeQuery(id+"F0.imprint","IMPRINT",EDGE,{"derivedFrom":subQ4}),-1.0]])]});}
            var Q2;
            Q2=makeQuery(id+"F0.imprint","IMPRINT",FACE,{"disambiguationData":[TD([[makeQuery(id+"F0.imprint","IMPRINT",EDGE,{"derivedFrom":sQuery(id+"F0.wireOp",EDGE,"E20")}),1.0]])]});
            var Q3;
            {var subQ3=sQuery(id+"F0.wireOp",EDGE,"E28");Q3=makeQuery(id+"F0.imprint","IMPRINT",FACE,{"disambiguationData":[TD([[makeQuery(id+"F0.imprint","IMPRINT",EDGE,{"derivedFrom":subQ3}),-1.0]])]});}
            var Q4;
            Q4=makeQuery(id+"F0.imprint","IMPRINT",FACE,{"disambiguationData":[TD([[makeQuery(id+"F0.imprint","IMPRINT",EDGE,{"derivedFrom":sQuery(id+"F0.wireOp",EDGE,"E117")}),-1.0]])]});
            var Q5;
            Q5=makeQuery(id+"F0.imprint","IMPRINT",FACE,{"disambiguationData":[TD([[makeQuery(id+"F0.imprint","IMPRINT",EDGE,{"derivedFrom":sQuery(id+"F0.wireOp",EDGE,"E120")}),-1.0]])]});
            var Q6;
            Q6=makeQuery(id+"F0.imprint","IMPRINT",FACE,{"disambiguationData":[TD([[makeQuery(id+"F0.imprint","IMPRINT",EDGE,{"derivedFrom":sQuery(id+"F0.wireOp",EDGE,"E102.left")}),1.0]])]});
            var Q7;
            Q7=makeQuery(id+"F0.imprint","IMPRINT",FACE,{"disambiguationData":[TD([[makeQuery(id+"F0.imprint","IMPRINT",EDGE,{"derivedFrom":sQuery(id+"F0.wireOp",EDGE,"E90")}),1.0]])]});
            var Q8;
            Q8=makeQuery(id+"F0.imprint","IMPRINT",FACE,{"disambiguationData":[TD([[makeQuery(id+"F0.imprint","IMPRINT",EDGE,{"derivedFrom":sQuery(id+"F0.wireOp",EDGE,"E111.bottom")}),1.0]])]});
            var Q9;
            Q9=makeQuery(id+"F0.imprint","IMPRINT",FACE,{"disambiguationData":[TD([[makeQuery(id+"F0.imprint","IMPRINT",EDGE,{"derivedFrom":sQuery(id+"F0.wireOp",EDGE,"E40.bottom")}),1.0]])]});
            var Q10;
            Q10=makeQuery(id+"F0.imprint","IMPRINT",FACE,{"disambiguationData":[TD([[makeQuery(id+"F0.imprint","IMPRINT",EDGE,{"derivedFrom":sQuery(id+"F0.wireOp",EDGE,"E65")}),1.0]])]});
            var Q11;
            Q11=makeQuery(id+"F0.imprint","IMPRINT",FACE,{"disambiguationData":[TD([[makeQuery(id+"F0.imprint","IMPRINT",EDGE,{"derivedFrom":sQuery(id+"F0.wireOp",EDGE,"E44")}),1.0]])]});
            var Q12;
            Q12=makeQuery(id+"F0.imprint","IMPRINT",FACE,{"disambiguationData":[TD([[makeQuery(id+"F0.imprint","IMPRINT",EDGE,{"derivedFrom":sQuery(id+"F0.wireOp",EDGE,"E42.left")}),1.0]])]});
            var Q13;
            Q13=makeQuery(id+"F0.imprint","IMPRINT",FACE,{"disambiguationData":[TD([[makeQuery(id+"F0.imprint","IMPRINT",EDGE,{"derivedFrom":sQuery(id+"F0.wireOp",EDGE,"E61")}),-1.0]])]});
            var Q14;
            Q14=makeQuery(id+"F0.imprint","IMPRINT",FACE,{"disambiguationData":[TD([[makeQuery(id+"F0.imprint","IMPRINT",EDGE,{"derivedFrom":sQuery(id+"F0.wireOp",EDGE,"E69.bottom")}),-1.0]])]});
            var Q15;
            {var subQ2=sQuery(id+"F0.wireOp",EDGE,"E76");Q15=makeQuery(id+"F0.imprint","IMPRINT",FACE,{"disambiguationData":[TD([[makeQuery(id+"F0.imprint","IMPRINT",EDGE,{"derivedFrom":subQ2}),-1.0]])]});}
            var Q16;
            Q16=makeQuery(id+"F0.imprint","IMPRINT",FACE,{"disambiguationData":[TD([[makeQuery(id+"F0.imprint","IMPRINT",EDGE,{"derivedFrom":sQuery(id+"F0.wireOp",EDGE,"E207.bottom")}),-1.0]])]});
            var Q17;
            Q17=makeQuery(id+"F0.imprint","IMPRINT",FACE,{"disambiguationData":[TD([[makeQuery(id+"F0.imprint","IMPRINT",EDGE,{"derivedFrom":sQuery(id+"F0.wireOp",EDGE,"E208.bottom")}),-1.0]])]});
            var Q18;
            {var subQ4=sQuery(id+"F0.wireOp",EDGE,"E209.bottom");Q18=makeQuery(id+"F0.imprint","IMPRINT",FACE,{"disambiguationData":[TD([[makeQuery(id+"F0.imprint","IMPRINT",EDGE,{"derivedFrom":subQ4}),-1.0]])]});}
            var Q19;
            Q19=makeQuery(id+"F0.imprint","IMPRINT",FACE,{"disambiguationData":[TD([[makeQuery(id+"F0.imprint","IMPRINT",EDGE,{"derivedFrom":sQuery(id+"F0.wireOp",EDGE,"E197")}),-1.0]])]});
            var Q20;
            Q20=makeQuery(id+"F0.imprint","IMPRINT",FACE,{"disambiguationData":[TD([[makeQuery(id+"F0.imprint","IMPRINT",EDGE,{"derivedFrom":sQuery(id+"F0.wireOp",EDGE,"E191")}),1.0]])]});
            var Q21;
            Q21=makeQuery(id+"F0.imprint","IMPRINT",FACE,{"disambiguationData":[TD([[makeQuery(id+"F0.imprint","IMPRINT",EDGE,{"derivedFrom":sQuery(id+"F0.wireOp",EDGE,"E183.MirrorCS")}),-1.0]])]});
            var Q22;
            {var subQ6=sQuery(id+"F0.wireOp",EDGE,"E167");Q22=makeQuery(id+"F0.imprint","IMPRINT",FACE,{"disambiguationData":[TD([[makeQuery(id+"F0.imprint","IMPRINT",EDGE,{"derivedFrom":subQ6}),-1.0]])]});}
            var Q23;
            Q23=makeQuery(id+"F0.imprint","IMPRINT",FACE,{"disambiguationData":[TD([[makeQuery(id+"F0.imprint","IMPRINT",EDGE,{"derivedFrom":sQuery(id+"F0.wireOp",EDGE,"E175")}),1.0]])]});
            var Q24;
            Q24=makeQuery(id+"F0.imprint","IMPRINT",FACE,{"disambiguationData":[TD([[makeQuery(id+"F0.imprint","IMPRINT",EDGE,{"derivedFrom":sQuery(id+"F0.wireOp",EDGE,"E228")}),1.0]])]});
            var Q25;
            Q25=makeQuery(id+"F0.imprint","IMPRINT",FACE,{"disambiguationData":[TD([[makeQuery(id+"F0.imprint","IMPRINT",EDGE,{"derivedFrom":sQuery(id+"F0.wireOp",EDGE,"E221")}),-1.0]])]});
            var Q26;
            {var subQ0=sQuery(id+"F0.wireOp",EDGE,"E210");Q26=makeQuery(id+"F0.imprint","IMPRINT",FACE,{"disambiguationData":[TD([[makeQuery(id+"F0.imprint","IMPRINT",EDGE,{"derivedFrom":subQ0}),1.0]])]});}
            var Q27;
            Q27=makeQuery(id+"F0.imprint","IMPRINT",FACE,{"disambiguationData":[TD([[makeQuery(id+"F0.imprint","IMPRINT",EDGE,{"derivedFrom":sQuery(id+"F0.wireOp",EDGE,"E217")}),-1.0]])]});
            var Q28;
            Q28=makeQuery(id+"F0.imprint","IMPRINT",FACE,{"disambiguationData":[TD([[makeQuery(id+"F0.imprint","IMPRINT",EDGE,{"derivedFrom":sQuery(id+"F0.wireOp",EDGE,"E234")}),-1.0]])]});
            var Q29;
            Q29=makeQuery(id+"F0.imprint","IMPRINT",FACE,{"disambiguationData":[TD([[makeQuery(id+"F0.imprint","IMPRINT",EDGE,{"derivedFrom":sQuery(id+"F0.wireOp",EDGE,"E241")}),1.0]])]});
            var Q30;
            Q30=makeQuery(id+"F0.imprint","IMPRINT",FACE,{"disambiguationData":[TD([[makeQuery(id+"F0.imprint","IMPRINT",EDGE,{"derivedFrom":sQuery(id+"F0.wireOp",EDGE,"E260")}),-1.0]])]});
            var Q31;
            {var subQ0=sQuery(id+"F0.wireOp",EDGE,"E253");Q31=makeQuery(id+"F0.imprint","IMPRINT",FACE,{"disambiguationData":[TD([[makeQuery(id+"F0.imprint","IMPRINT",EDGE,{"derivedFrom":subQ0}),1.0]])]});}
            var Q32;
            {var subQ0=sQuery(id+"F0.wireOp",EDGE,"E127.left");Q32=makeQuery(id+"F0.imprint","IMPRINT",FACE,{"disambiguationData":[TD([[makeQuery(id+"F0.imprint","IMPRINT",EDGE,{"derivedFrom":subQ0}),1.0]])]});}
            extrude(context, id + "F3", {"entities" : qUnion([Q0, Q1, Q2, Q3, Q4, Q5, Q6, Q7, Q8, Q9, Q10, Q11, Q12, Q13, Q14, Q15, Q16, Q17, Q18, Q19, Q20, Q21, Q22, Q23, Q24, Q25, Q26, Q27, Q28, Q29, Q30, Q31, Q32]), "depth" : 30.48 * mm, "offsetDistance" : 25.4 * mm});
        }
    });
